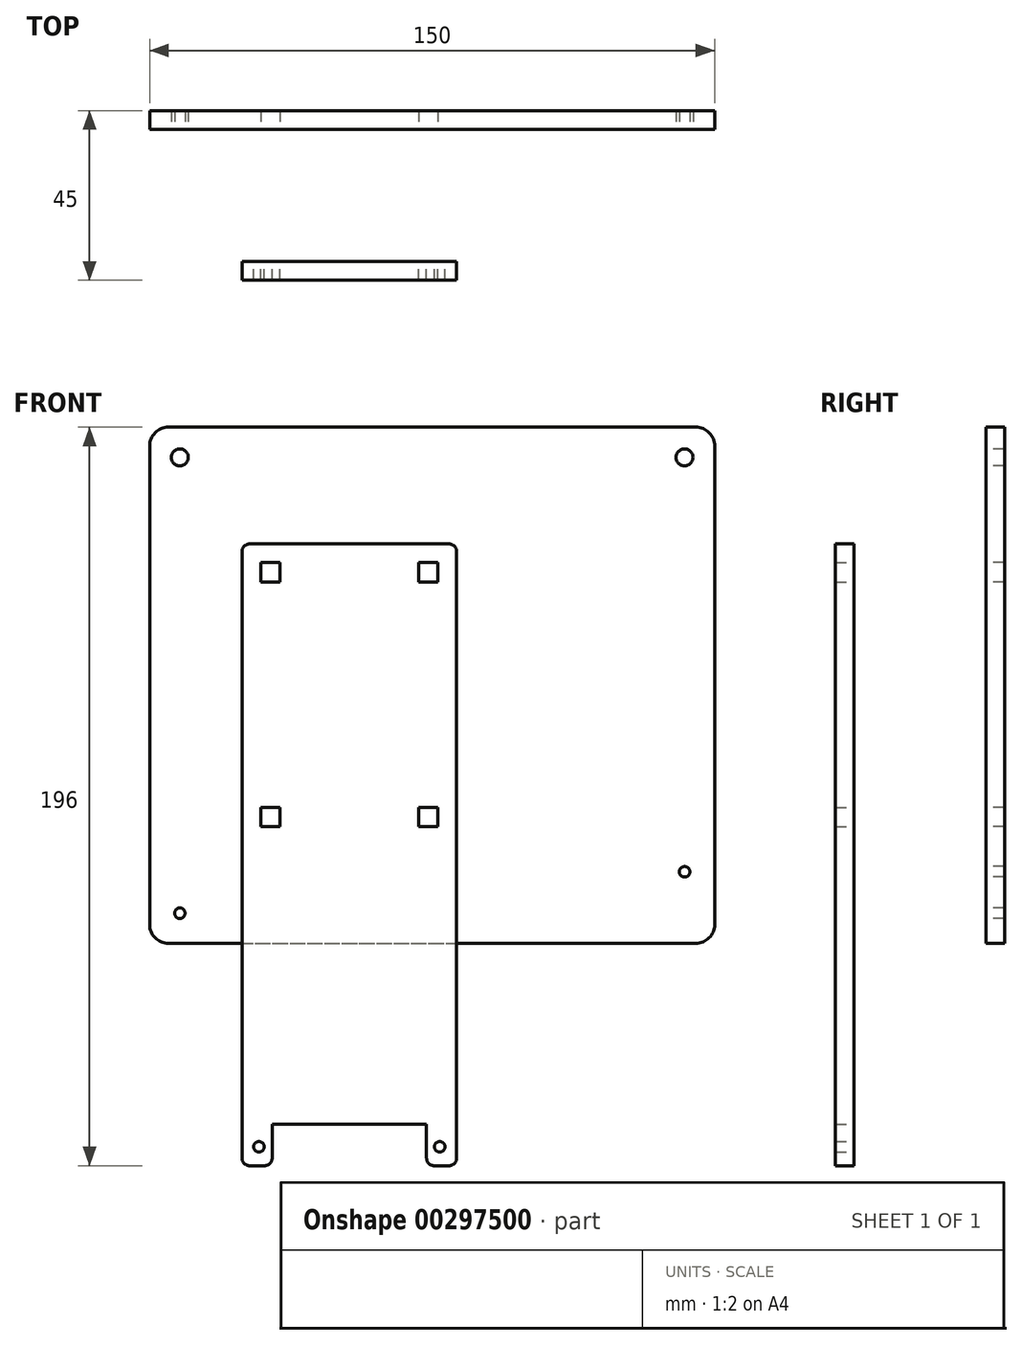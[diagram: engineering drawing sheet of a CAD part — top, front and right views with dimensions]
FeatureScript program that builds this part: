
annotation { "Feature Type Name" : "Feature", "Feature Type Description" : "" }
export const myFeature = defineFeature(function(context is Context, id is Id, definition is map)
    precondition{}
    {
        {
            var Q0;
            Q0=qCreatedBy(makeId("Front.planeOp"),FACE);
            var sketch = newSketch(context, id + "F0", { "sketchPlane" : qUnion([Q0])});
            skLineSegment(sketch, "E0", {"start": v(-53, 64) * mm, "end": v(-53, 191) * mm});
            skCircle(sketch, "E1", {"center": v(-45, 67) * mm, "radius": 1.4 * mm});
            skCircle(sketch, "E2", {"center": v(89, 78) * mm, "radius": 1.4 * mm});
            skLineSegment(sketch, "E3", {"start": v(97, 191) * mm, "end": v(97, 64) * mm});
            skLineSegment(sketch, "E4", {"start": v(-48, 196) * mm, "end": v(92, 196) * mm});
            skArc(sketch, "E5.filletArc", {"start": v(-48, 196) * mm, "mid": v(-51.54, 194.54) * mm, "end": v(-53, 191) * mm});
            skArc(sketch, "E6.filletArc", {"start": v(97, 191) * mm, "mid": v(95.54, 194.54) * mm, "end": v(92, 196) * mm});
            skCircle(sketch, "E7", {"center": v(-45, 188) * mm, "radius": 2.25 * mm});
            skCircle(sketch, "E8", {"center": v(89, 188) * mm, "radius": 2.25 * mm});
            skLineSegment(sketch, "E9", {"start": v(-48, 59) * mm, "end": v(92, 59) * mm});
            skArc(sketch, "E10.filletArc", {"start": v(-53, 64) * mm, "mid": v(-51.54, 60.46) * mm, "end": v(-48, 59) * mm});
            skArc(sketch, "E11.filletArc", {"start": v(92, 59) * mm, "mid": v(95.54, 60.46) * mm, "end": v(97, 64) * mm});
            skPoint(sketch, "E12", {"position": v(0, 0) * mm});
            skLineSegment(sketch, "E13.bottom", {"start": v(-23.55, 160.05) * mm, "end": v(-18.45, 160.05) * mm});
            skLineSegment(sketch, "E13.top", {"start": v(-23.55, 154.95) * mm, "end": v(-18.45, 154.95) * mm});
            skLineSegment(sketch, "E13.left", {"start": v(-23.55, 160.05) * mm, "end": v(-23.55, 154.95) * mm});
            skLineSegment(sketch, "E13.right", {"start": v(-18.45, 160.05) * mm, "end": v(-18.45, 154.95) * mm});
            skLineSegment(sketch, "E14.bottom", {"start": v(18.45, 160.05) * mm, "end": v(23.55, 160.05) * mm});
            skLineSegment(sketch, "E14.top", {"start": v(18.45, 154.95) * mm, "end": v(23.55, 154.95) * mm});
            skLineSegment(sketch, "E14.left", {"start": v(18.45, 160.05) * mm, "end": v(18.45, 154.95) * mm});
            skLineSegment(sketch, "E14.right", {"start": v(23.55, 160.05) * mm, "end": v(23.55, 154.95) * mm});
            skLineSegment(sketch, "E15.bottom", {"start": v(-23.55, 95.05) * mm, "end": v(-18.45, 95.05) * mm});
            skLineSegment(sketch, "E15.top", {"start": v(-23.55, 89.95) * mm, "end": v(-18.45, 89.95) * mm});
            skLineSegment(sketch, "E15.left", {"start": v(-23.55, 95.05) * mm, "end": v(-23.55, 89.95) * mm});
            skLineSegment(sketch, "E15.right", {"start": v(-18.45, 95.05) * mm, "end": v(-18.45, 89.95) * mm});
            skLineSegment(sketch, "E16.bottom", {"start": v(23.55, 95.05) * mm, "end": v(18.45, 95.05) * mm});
            skLineSegment(sketch, "E16.top", {"start": v(23.55, 89.95) * mm, "end": v(18.45, 89.95) * mm});
            skLineSegment(sketch, "E16.left", {"start": v(23.55, 95.05) * mm, "end": v(23.55, 89.95) * mm});
            skLineSegment(sketch, "E16.right", {"start": v(18.45, 95.05) * mm, "end": v(18.45, 89.95) * mm});
            skPoint(sketch, "E17", {"position": v(-21, 160.05) * mm});
            skPoint(sketch, "E18", {"position": v(21, 160.05) * mm});
            skPoint(sketch, "E19", {"position": v(23.55, 157.5) * mm});
            skPoint(sketch, "E20", {"position": v(-23.55, 157.5) * mm});
            skPoint(sketch, "E21", {"position": v(-23.55, 92.5) * mm});
            skPoint(sketch, "E22", {"position": v(18.45, 92.5) * mm});
            skPoint(sketch, "E23.middle.positionSnap0", {"position": v(23.55, 92.5) * mm});
            skPoint(sketch, "E23.centerSnap0", {"position": v(23.55, 92.5) * mm});
            skPoint(sketch, "E24", {"position": v(60.49, 176) * mm});
            skSolve(sketch);
        }
        {
            var Q0;
            Q0=qCreatedBy(makeId("Front.planeOp"),FACE);
            cPlane(context, id + "F1", {"entities" : qUnion([Q0]), "cplaneType" : CPlaneType.OFFSET, "offset" : (17 + 18) * mm, "width" : 150 * mm, "height" : 150 * mm});
        }
        {
            var Q0;
            Q0=qCreatedBy(id+"F1.planeOp",FACE);
            var sketch = newSketch(context, id + "F2", { "sketchPlane" : qUnion([Q0])});
            skPoint(sketch, "E25", {"position": v(0, 0) * mm});
            skCircle(sketch, "E26", {"center": v(-24, 5) * mm, "radius": 1.4 * mm});
            skCircle(sketch, "E27", {"center": v(24, 5) * mm, "radius": 1.4 * mm});
            skLineSegment(sketch, "E28", {"start": v(-26.5, 0) * mm, "end": v(-22.5, 0) * mm});
            skLineSegment(sketch, "E29.trimOffspring", {"start": v(22.5, 0) * mm, "end": v(26.5, 0) * mm});
            skLineSegment(sketch, "E30.top", {"start": v(-20.5, 11) * mm, "end": v(20.5, 11) * mm});
            skLineSegment(sketch, "E30.left", {"start": v(-20.5, 2) * mm, "end": v(-20.5, 11) * mm});
            skLineSegment(sketch, "E30.right", {"start": v(20.5, 2) * mm, "end": v(20.5, 11) * mm});
            skPoint(sketch, "E30.middle", {"position": v(0, 5.5) * mm});
            skLineSegment(sketch, "E31", {"start": v(-28.5, 2) * mm, "end": v(-28.5, 163) * mm});
            skLineSegment(sketch, "E32", {"start": v(-26.5, 165) * mm, "end": v(26.5, 165) * mm});
            skLineSegment(sketch, "E33", {"start": v(28.5, 163) * mm, "end": v(28.5, 2) * mm});
            skLineSegment(sketch, "E34.bottom", {"start": v(-23.55, 160.05) * mm, "end": v(-18.45, 160.05) * mm});
            skLineSegment(sketch, "E34.top", {"start": v(-23.55, 154.95) * mm, "end": v(-18.45, 154.95) * mm});
            skLineSegment(sketch, "E34.left", {"start": v(-23.55, 160.05) * mm, "end": v(-23.55, 154.95) * mm});
            skLineSegment(sketch, "E34.right", {"start": v(-18.45, 160.05) * mm, "end": v(-18.45, 154.95) * mm});
            skLineSegment(sketch, "E35.bottom", {"start": v(18.45, 160.05) * mm, "end": v(23.55, 160.05) * mm});
            skLineSegment(sketch, "E35.top", {"start": v(18.45, 154.95) * mm, "end": v(23.55, 154.95) * mm});
            skLineSegment(sketch, "E35.left", {"start": v(18.45, 160.05) * mm, "end": v(18.45, 154.95) * mm});
            skLineSegment(sketch, "E35.right", {"start": v(23.55, 160.05) * mm, "end": v(23.55, 154.95) * mm});
            skLineSegment(sketch, "E36.bottom", {"start": v(-23.55, 95.05) * mm, "end": v(-18.45, 95.05) * mm});
            skLineSegment(sketch, "E36.top", {"start": v(-23.55, 89.95) * mm, "end": v(-18.45, 89.95) * mm});
            skLineSegment(sketch, "E36.left", {"start": v(-23.55, 95.05) * mm, "end": v(-23.55, 89.95) * mm});
            skLineSegment(sketch, "E36.right", {"start": v(-18.45, 95.05) * mm, "end": v(-18.45, 89.95) * mm});
            skLineSegment(sketch, "E37.bottom", {"start": v(23.55, 95.05) * mm, "end": v(18.45, 95.05) * mm});
            skLineSegment(sketch, "E37.top", {"start": v(23.55, 89.95) * mm, "end": v(18.45, 89.95) * mm});
            skLineSegment(sketch, "E37.left", {"start": v(23.55, 95.05) * mm, "end": v(23.55, 89.95) * mm});
            skLineSegment(sketch, "E37.right", {"start": v(18.45, 95.05) * mm, "end": v(18.45, 89.95) * mm});
            skPoint(sketch, "E38.visualSharp", {"position": v(-28.5, 0) * mm});
            skArc(sketch, "E38.filletArc", {"start": v(-28.5, 2) * mm, "mid": v(-27.91, 0.59) * mm, "end": v(-26.5, 0) * mm});
            skPoint(sketch, "E39.visualSharp", {"position": v(-20.5, 0) * mm});
            skArc(sketch, "E39.filletArc", {"start": v(-22.5, 0) * mm, "mid": v(-21.09, 0.59) * mm, "end": v(-20.5, 2) * mm});
            skPoint(sketch, "E40.visualSharp", {"position": v(20.5, 0) * mm});
            skArc(sketch, "E40.filletArc", {"start": v(20.5, 2) * mm, "mid": v(21.09, 0.59) * mm, "end": v(22.5, 0) * mm});
            skPoint(sketch, "E41.visualSharp", {"position": v(28.5, 0) * mm});
            skArc(sketch, "E41.filletArc", {"start": v(26.5, 0) * mm, "mid": v(27.91, 0.59) * mm, "end": v(28.5, 2) * mm});
            skPoint(sketch, "E42.visualSharp", {"position": v(-28.5, 165) * mm});
            skArc(sketch, "E42.filletArc", {"start": v(-26.5, 165) * mm, "mid": v(-27.91, 164.41) * mm, "end": v(-28.5, 163) * mm});
            skPoint(sketch, "E43", {"position": v(-21, 160.05) * mm});
            skPoint(sketch, "E44", {"position": v(21, 160.05) * mm});
            skPoint(sketch, "E45", {"position": v(23.55, 157.5) * mm});
            skPoint(sketch, "E46", {"position": v(-23.55, 157.5) * mm});
            skPoint(sketch, "E47", {"position": v(-23.55, 92.5) * mm});
            skPoint(sketch, "E48", {"position": v(18.45, 92.5) * mm});
            skLineSegment(sketch, "E49", {"start": v(38.5, 165) * mm, "end": v(38.5, 160) * mm});
            skLineSegment(sketch, "E50.bottom", {"start": v(38.5, 155) * mm, "end": v(33.5, 155) * mm});
            skLineSegment(sketch, "E50.top", {"start": v(38.5, 160) * mm, "end": v(33.5, 160) * mm});
            skLineSegment(sketch, "E50.right", {"start": v(33.5, 155) * mm, "end": v(33.5, 160) * mm});
            skPoint(sketch, "E50.middle", {"position": v(36, 157.5) * mm});
            skLineSegment(sketch, "E51.bottom", {"start": v(38.5, 90) * mm, "end": v(33.5, 90) * mm});
            skLineSegment(sketch, "E51.top", {"start": v(38.5, 95) * mm, "end": v(33.5, 95) * mm});
            skLineSegment(sketch, "E51.right", {"start": v(33.5, 90) * mm, "end": v(33.5, 95) * mm});
            skPoint(sketch, "E51.middle", {"position": v(36, 92.5) * mm});
            skPoint(sketch, "E51.middle.positionSnap0", {"position": v(23.55, 92.5) * mm});
            skPoint(sketch, "E51.centerSnap0", {"position": v(23.55, 92.5) * mm});
            skLineSegment(sketch, "E52.bottom", {"start": v(-40.5, 160) * mm, "end": v(-35.5, 160) * mm});
            skLineSegment(sketch, "E52.top", {"start": v(-40.5, 155) * mm, "end": v(-35.5, 155) * mm});
            skLineSegment(sketch, "E52.right", {"start": v(-35.5, 160) * mm, "end": v(-35.5, 155) * mm});
            skPoint(sketch, "E52.middle", {"position": v(-38, 157.5) * mm});
            skLineSegment(sketch, "E53.bottom", {"start": v(-40.5, 95) * mm, "end": v(-35.5, 95) * mm});
            skLineSegment(sketch, "E53.top", {"start": v(-40.5, 90) * mm, "end": v(-35.5, 90) * mm});
            skLineSegment(sketch, "E53.right", {"start": v(-35.5, 95) * mm, "end": v(-35.5, 90) * mm});
            skPoint(sketch, "E53.middle", {"position": v(-38, 92.5) * mm});
            skLineSegment(sketch, "E54.trimOffspring", {"start": v(38.5, 155) * mm, "end": v(38.5, 95) * mm});
            skLineSegment(sketch, "E55.trimOffspring", {"start": v(38.5, 90) * mm, "end": v(38.5, 85) * mm});
            skLineSegment(sketch, "E56", {"start": v(38.5, 165) * mm, "end": v(73.5, 165) * mm});
            skLineSegment(sketch, "E57", {"start": v(73.5, 165) * mm, "end": v(73.5, 160) * mm});
            skLineSegment(sketch, "E58", {"start": v(73.5, 160) * mm, "end": v(78.5, 160) * mm});
            skLineSegment(sketch, "E59", {"start": v(78.5, 160) * mm, "end": v(78.5, 155) * mm});
            skLineSegment(sketch, "E60", {"start": v(78.5, 155) * mm, "end": v(73.5, 155) * mm});
            skLineSegment(sketch, "E61", {"start": v(73.5, 155) * mm, "end": v(73.5, 95) * mm});
            skLineSegment(sketch, "E62", {"start": v(73.5, 95) * mm, "end": v(78.5, 95) * mm});
            skLineSegment(sketch, "E63", {"start": v(78.5, 95) * mm, "end": v(78.5, 90) * mm});
            skLineSegment(sketch, "E64", {"start": v(78.5, 90) * mm, "end": v(73.5, 90) * mm});
            skLineSegment(sketch, "E65", {"start": v(73.5, 90) * mm, "end": v(73.5, 85) * mm});
            skLineSegment(sketch, "E66", {"start": v(73.5, 85) * mm, "end": v(38.5, 85) * mm});
            skLineSegment(sketch, "E67.trimOffspring", {"start": v(-40.5, 155) * mm, "end": v(-40.5, 95) * mm});
            skPoint(sketch, "E68.start.orphan", {"position": v(-40.5, 165) * mm});
            skLineSegment(sketch, "E69.trimOffspring", {"start": v(-40.5, 90) * mm, "end": v(-40.5, 85) * mm});
            skLineSegment(sketch, "E70", {"start": v(-40.5, 160) * mm, "end": v(-40.5, 165) * mm});
            skLineSegment(sketch, "E71", {"start": v(-40.5, 165) * mm, "end": v(-75.5, 165) * mm});
            skLineSegment(sketch, "E72", {"start": v(-75.5, 165) * mm, "end": v(-75.5, 160) * mm});
            skLineSegment(sketch, "E73", {"start": v(-75.5, 160) * mm, "end": v(-80.5, 160) * mm});
            skLineSegment(sketch, "E74", {"start": v(-80.5, 160) * mm, "end": v(-80.5, 155) * mm});
            skPoint(sketch, "E74.endSnap0", {"position": v(-38, 155) * mm});
            skLineSegment(sketch, "E75", {"start": v(-80.5, 155) * mm, "end": v(-75.5, 155) * mm});
            skLineSegment(sketch, "E76", {"start": v(-75.5, 155) * mm, "end": v(-75.5, 95) * mm});
            skLineSegment(sketch, "E77", {"start": v(-75.5, 95) * mm, "end": v(-80.5, 95) * mm});
            skLineSegment(sketch, "E78", {"start": v(-80.5, 95) * mm, "end": v(-80.5, 90) * mm});
            skLineSegment(sketch, "E79", {"start": v(-80.5, 90) * mm, "end": v(-75.5, 90) * mm});
            skLineSegment(sketch, "E80", {"start": v(-75.5, 90) * mm, "end": v(-75.5, 85) * mm});
            skLineSegment(sketch, "E81", {"start": v(-75.5, 85) * mm, "end": v(-40.5, 85) * mm});
            skPoint(sketch, "E82", {"position": v(0, 11) * mm});
            skPoint(sketch, "E83.visualSharp", {"position": v(28.5, 165) * mm});
            skArc(sketch, "E83.filletArc", {"start": v(28.5, 163) * mm, "mid": v(27.91, 164.41) * mm, "end": v(26.5, 165) * mm});
            skSolve(sketch);
        }
        {
            var Q0;
            Q0=makeQuery(id+"F2.imprint","IMPRINT",FACE,{"disambiguationData":[TD([[makeQuery(id+"F2.imprint","IMPRINT",EDGE,{"derivedFrom":sQuery(id+"F2.wireOp",EDGE,"E26")}),-1.0]])]});
            extrude(context, id + "F3", {"entities" : qUnion([Q0]), "depth" : 5 * mm});
        }
        {
            var Q0;
            Q0=makeQuery(id+"F0.imprint","IMPRINT",FACE,{"disambiguationData":[TD([[makeQuery(id+"F0.imprint","IMPRINT",EDGE,{"derivedFrom":sQuery(id+"F0.wireOp",EDGE,"E0")}),-1.0]])]});
            extrude(context, id + "F4", {"entities" : qUnion([Q0]), "oppositeDirection" : true, "depth" : 5 * mm});
        }
    });
